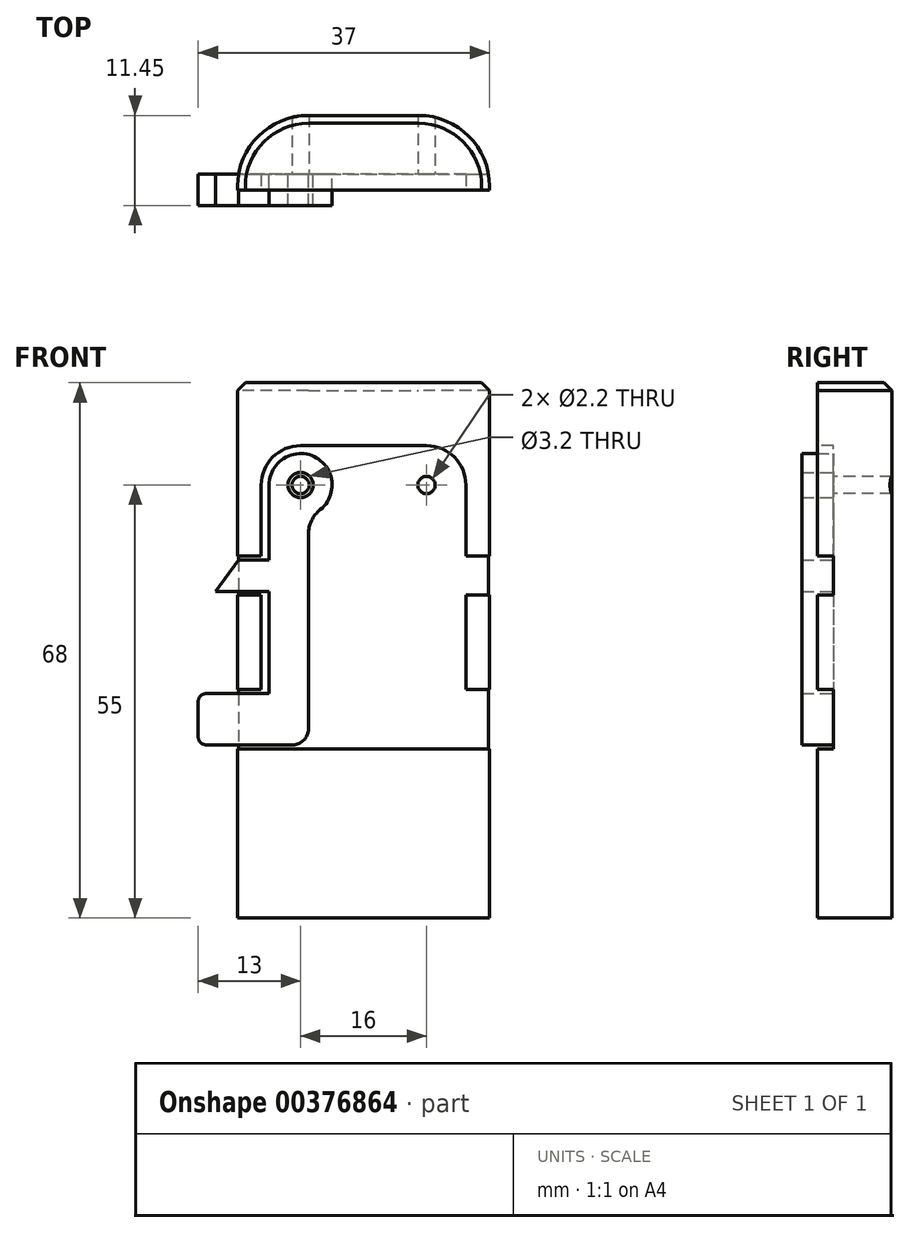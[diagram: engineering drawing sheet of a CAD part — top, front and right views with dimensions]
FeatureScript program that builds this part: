
annotation { "Feature Type Name" : "Feature", "Feature Type Description" : "" }
export const myFeature = defineFeature(function(context is Context, id is Id, definition is map)
    precondition{}
    {
        {
            var Q0;
            Q0=qCreatedBy(makeId("Top.planeOp"),FACE);
            var sketch = newSketch(context, id + "F0", { "sketchPlane" : qUnion([Q0])});
            skLineSegment(sketch, "E0.bottom", {"start": v(7, -9.5) * mm, "end": v(-7, -9.5) * mm});
            skLineSegment(sketch, "E0.top", {"start": v(7, 9.5) * mm, "end": v(-7, 9.5) * mm});
            skLineSegment(sketch, "E0.left", {"start": v(16, -0.5) * mm, "end": v(16, 0.5) * mm});
            skLineSegment(sketch, "E0.right", {"start": v(-16, -0.5) * mm, "end": v(-16, 0.5) * mm});
            skPoint(sketch, "E0.middle", {"position": v(0, 0) * mm});
            skPoint(sketch, "E1.visualSharp", {"position": v(-16, 9.5) * mm});
            skArc(sketch, "E1.filletArc", {"start": v(-7, 9.5) * mm, "mid": v(-13.36, 6.86) * mm, "end": v(-16, 0.5) * mm});
            skPoint(sketch, "E2.visualSharp", {"position": v(-16, -9.5) * mm});
            skArc(sketch, "E2.filletArc", {"start": v(-16, -0.5) * mm, "mid": v(-13.36, -6.86) * mm, "end": v(-7, -9.5) * mm});
            skPoint(sketch, "E3.visualSharp", {"position": v(16, -9.5) * mm});
            skArc(sketch, "E3.filletArc", {"start": v(7, -9.5) * mm, "mid": v(13.36, -6.86) * mm, "end": v(16, -0.5) * mm});
            skPoint(sketch, "E4.visualSharp", {"position": v(16, 9.5) * mm});
            skArc(sketch, "E4.filletArc", {"start": v(16, 0.5) * mm, "mid": v(13.36, 6.86) * mm, "end": v(7, 9.5) * mm});
            skSolve(sketch);
        }
        {
            var Q0;
            Q0 = qSketchRegion(id + "F0", true);
            extrude(context, id + "F1", {"entities" : qUnion([Q0]), "endBound" : BoundingType.SYMMETRIC, "depth" : 68 * mm});
        }
        {
            var Q0;
            Q0=makeQuery(id+"F1.opExtrude","CAP_FACE",FACE,{"disambiguationData":[OSD([sQuery(id+"F0.wireOp",EDGE,"E0.bottom"),sQuery(id+"F0.wireOp",EDGE,"E0.top"),sQuery(id+"F0.wireOp",EDGE,"E0.left"),sQuery(id+"F0.wireOp",EDGE,"E0.right"),sQuery(id+"F0.wireOp",EDGE,"E1.filletArc"),sQuery(id+"F0.wireOp",EDGE,"E2.filletArc"),sQuery(id+"F0.wireOp",EDGE,"E3.filletArc"),sQuery(id+"F0.wireOp",EDGE,"E4.filletArc")])],"isStart":false});
            chamfer(context, id + "F2", {"entities" : qUnion([Q0]), "width" : 1 * mm, "tangentPropagation" : true});
        }
        {
            var Q0;
            Q0=qCreatedBy(makeId("Top.planeOp"),FACE);
            var sketch = newSketch(context, id + "F3", { "sketchPlane" : qUnion([Q0])});
            skLineSegment(sketch, "E5.bottom", {"start": v(-35.43, 0) * mm, "end": v(39.3, 0) * mm});
            skLineSegment(sketch, "E5.top", {"start": v(-35.43, -20.34) * mm, "end": v(39.3, -20.34) * mm});
            skLineSegment(sketch, "E5.left", {"start": v(-35.43, 0) * mm, "end": v(-35.43, -20.34) * mm});
            skLineSegment(sketch, "E5.right", {"start": v(39.3, 0) * mm, "end": v(39.3, -20.34) * mm});
            skSolve(sketch);
        }
        {
            var Q0;
            Q0 = qSketchRegion(id + "F3", true);
            extrude(context, id + "F4", {"entities" : qUnion([Q0]), "operationType" : NewBodyOperationType.REMOVE, "endBound" : BoundingType.SYMMETRIC, "depth" : 70 * mm});
        }
        {
            var Q0;
            Q0=qCreatedBy(makeId("Front.planeOp"),FACE);
            var sketch = newSketch(context, id + "F5", { "sketchPlane" : qUnion([Q0])});
            skLineSegment(sketch, "E6.top", {"start": v(8, 26) * mm, "end": v(-8, 26) * mm});
            skPoint(sketch, "E6.middle", {"position": v(0, 0) * mm});
            skPoint(sketch, "E7.visualSharp", {"position": v(-13, 26) * mm});
            skArc(sketch, "E7.filletArc", {"start": v(-8, 26) * mm, "mid": v(-11.54, 24.54) * mm, "end": v(-13, 21) * mm});
            skPoint(sketch, "E8.visualSharp", {"position": v(13, 26) * mm});
            skArc(sketch, "E8.filletArc", {"start": v(13, 21) * mm, "mid": v(11.54, 24.54) * mm, "end": v(8, 26) * mm});
            skLineSegment(sketch, "E9.bottom", {"start": v(30, 7) * mm, "end": v(13, 7) * mm});
            skLineSegment(sketch, "E9.top", {"start": v(30, 12) * mm, "end": v(13, 12) * mm});
            skLineSegment(sketch, "E9.left", {"start": v(30, 7) * mm, "end": v(30, 12) * mm});
            skLineSegment(sketch, "E9.right", {"start": v(-30, 7) * mm, "end": v(-30, 12) * mm});
            skPoint(sketch, "E9.middle", {"position": v(0, 9.5) * mm});
            skLineSegment(sketch, "E10.trimOffspring", {"start": v(-13, 12) * mm, "end": v(-13, 21) * mm});
            skLineSegment(sketch, "E11.trimOffspring", {"start": v(-13, 12) * mm, "end": v(-30, 12) * mm});
            skLineSegment(sketch, "E12.trimOffspring", {"start": v(13, 12) * mm, "end": v(13, 21) * mm});
            skLineSegment(sketch, "E13.trimOffspring", {"start": v(-13, 7) * mm, "end": v(-30, 7) * mm});
            skCircle(sketch, "E14", {"center": v(-8, 21) * mm, "radius": 1.1 * mm});
            skCircle(sketch, "E15", {"center": v(8, 21) * mm, "radius": 1.1 * mm});
            skLineSegment(sketch, "E16.bottom", {"start": v(-20.45, -5) * mm, "end": v(-13, -5) * mm});
            skLineSegment(sketch, "E16.top", {"start": v(-20.45, -12.5) * mm, "end": v(19.97, -12.5) * mm});
            skLineSegment(sketch, "E16.left", {"start": v(-20.45, -5) * mm, "end": v(-20.45, -12.5) * mm});
            skLineSegment(sketch, "E16.right", {"start": v(19.97, -5) * mm, "end": v(19.97, -12.5) * mm});
            skLineSegment(sketch, "E17.trimOffspring", {"start": v(-13, -5) * mm, "end": v(-13, 7) * mm});
            skLineSegment(sketch, "E18.trimOffspring", {"start": v(13, -5) * mm, "end": v(19.97, -5) * mm});
            skLineSegment(sketch, "E19.trimOffspring", {"start": v(13, -5) * mm, "end": v(13, 7) * mm});
            skPoint(sketch, "E6.bottom.end.orphan", {"position": v(-13, -26) * mm});
            skPoint(sketch, "E6.bottom.start.orphan", {"position": v(13, -26) * mm});
            skSolve(sketch);
        }
        {
            var Q0;
            Q0 = qSketchRegion(id + "F5", true);
            var Q1;
            Q1=makeQuery(id+"F5.imprint","IMPRINT",FACE,{"disambiguationData":[TD([[makeQuery(id+"F5.imprint","IMPRINT",EDGE,{"derivedFrom":sQuery(id+"F5.wireOp",EDGE,"E14")}),1.0]])]});
            var Q2;
            Q2=makeQuery(id+"F5.imprint","IMPRINT",FACE,{"disambiguationData":[TD([[makeQuery(id+"F5.imprint","IMPRINT",EDGE,{"derivedFrom":sQuery(id+"F5.wireOp",EDGE,"E15")}),1.0]])]});
            extrude(context, id + "F6", {"entities" : qUnion([Q0, Q1, Q2]), "operationType" : NewBodyOperationType.REMOVE, "oppositeDirection" : true, "depth" : 2.05 * mm});
        }
        {
            var Q0;
            Q0=makeQuery(id+"F5.imprint","IMPRINT",FACE,{"disambiguationData":[TD([[makeQuery(id+"F5.imprint","IMPRINT",EDGE,{"derivedFrom":sQuery(id+"F5.wireOp",EDGE,"E14")}),1.0]])]});
            var Q1;
            Q1=makeQuery(id+"F5.imprint","IMPRINT",FACE,{"disambiguationData":[TD([[makeQuery(id+"F5.imprint","IMPRINT",EDGE,{"derivedFrom":sQuery(id+"F5.wireOp",EDGE,"E15")}),1.0]])]});
            extrude(context, id + "F7", {"entities" : qUnion([Q0, Q1]), "operationType" : NewBodyOperationType.REMOVE, "oppositeDirection" : true, "depth" : 25 * mm});
        }
        {
            var Q0;
            Q0=makeQuery(id+"F6.boolean.opBoolean","COPY",FACE,{"derivedFrom":makeQuery(id+"F6.opExtrude","CAP_FACE",FACE,{"disambiguationData":[OSD([sQuery(id+"F5.wireOp",EDGE,"E6.top"),sQuery(id+"F5.wireOp",EDGE,"E7.filletArc"),sQuery(id+"F5.wireOp",EDGE,"E8.filletArc"),sQuery(id+"F5.wireOp",EDGE,"E9.bottom"),sQuery(id+"F5.wireOp",EDGE,"E9.top"),sQuery(id+"F5.wireOp",EDGE,"E9.left"),sQuery(id+"F5.wireOp",EDGE,"E9.right"),sQuery(id+"F5.wireOp",EDGE,"E10.trimOffspring"),sQuery(id+"F5.wireOp",EDGE,"E11.trimOffspring"),sQuery(id+"F5.wireOp",EDGE,"E12.trimOffspring"),sQuery(id+"F5.wireOp",EDGE,"E13.trimOffspring"),sQuery(id+"F5.wireOp",EDGE,"E16.bottom"),sQuery(id+"F5.wireOp",EDGE,"E16.top"),sQuery(id+"F5.wireOp",EDGE,"E16.left"),sQuery(id+"F5.wireOp",EDGE,"E16.right"),sQuery(id+"F5.wireOp",EDGE,"E17.trimOffspring"),sQuery(id+"F5.wireOp",EDGE,"E18.trimOffspring"),sQuery(id+"F5.wireOp",EDGE,"E19.trimOffspring")])],"isStart":false})});
            var sketch = newSketch(context, id + "F8", { "sketchPlane" : qUnion([Q0])});
            skCircle(sketch, "E20", {"center": v(-8, 21) * mm, "radius": 1.6 * mm});
            skLineSegment(sketch, "E21.bottom", {"start": v(-15.87, 11.5) * mm, "end": v(-12, 11.5) * mm});
            skLineSegment(sketch, "E21.top", {"start": v(-18.8, 7.5) * mm, "end": v(-12, 7.5) * mm});
            skLineSegment(sketch, "E22", {"start": v(-18.8, 7.5) * mm, "end": v(-15.87, 11.5) * mm});
            skLineSegment(sketch, "E23.bottom", {"start": v(-20, -5.5) * mm, "end": v(-12, -5.5) * mm});
            skLineSegment(sketch, "E23.top", {"start": v(-20, -12) * mm, "end": v(-9, -12) * mm});
            skLineSegment(sketch, "E23.left", {"start": v(-21, -6.5) * mm, "end": v(-21, -11) * mm});
            skLineSegment(sketch, "E24.left", {"start": v(-12, 21) * mm, "end": v(-12, 11.5) * mm});
            skPoint(sketch, "E25.visualSharp", {"position": v(-4, -12) * mm});
            skPoint(sketch, "E26.visualSharp", {"position": v(-21, -12) * mm});
            skArc(sketch, "E26.filletArc", {"start": v(-21, -11) * mm, "mid": v(-20.7, -11.7) * mm, "end": v(-20, -12) * mm});
            skPoint(sketch, "E27.visualSharp", {"position": v(-21, -5.5) * mm});
            skArc(sketch, "E27.filletArc", {"start": v(-20, -5.5) * mm, "mid": v(-20.7, -5.8) * mm, "end": v(-21, -6.5) * mm});
            skLineSegment(sketch, "E28.trimOffspring", {"start": v(-12, 7.5) * mm, "end": v(-12, -5.5) * mm});
            skLineSegment(sketch, "E29", {"start": v(-7, 14.76) * mm, "end": v(-7, 1) * mm});
            skPoint(sketch, "E30.orphan", {"position": v(-9.1, -12) * mm});
            skArc(sketch, "E31", {"start": v(-5.5, 17.88) * mm, "mid": v(-6.27, 24.6) * mm, "end": v(-12, 21) * mm});
            skPoint(sketch, "E32.visualSharp", {"position": v(-7, 17.13) * mm});
            skArc(sketch, "E32.filletArc", {"start": v(-5.5, 17.88) * mm, "mid": v(-6.6, 16.49) * mm, "end": v(-7, 14.76) * mm});
            skPoint(sketch, "E33.visualSharp", {"position": v(-7, -12) * mm});
            skArc(sketch, "E33.filletArc", {"start": v(-9, -12) * mm, "mid": v(-7.59, -11.41) * mm, "end": v(-7, -10) * mm});
            skPoint(sketch, "E34.middle", {"position": v(0, 0) * mm});
            skPoint(sketch, "E35.orphan", {"position": v(-10, 1) * mm});
            skPoint(sketch, "E36.orphan", {"position": v(-10, -1) * mm});
            skLineSegment(sketch, "E37.trimOffspring", {"start": v(-7, -1) * mm, "end": v(-7, -10) * mm});
            skPoint(sketch, "E34.left.end.orphan", {"position": v(10, 1) * mm});
            skPoint(sketch, "E34.left.start.orphan", {"position": v(10, -1) * mm});
            skLineSegment(sketch, "E38", {"start": v(-7, 1) * mm, "end": v(-7, -1) * mm});
            skSolve(sketch);
        }
        {
            var Q0;
            Q0 = qSketchRegion(id + "F8", true);
            extrude(context, id + "F9", {"entities" : qUnion([Q0]), "depth" : 4 * mm});
        }
    });
